# Revit family: FantiniCosmi_BIM_AP3102
name_source: partatom
category: Generic Models
units: mm (PartAtom-declared; Revit-internal decimal feet)

## family parameters
Always vertical = Yes
Can host rebar = No
Cut with Voids When Loaded = No
Part Type = Normal
Room Calculation Point = No
Round Connector Dimension = Use Diameter
Shared = No
Work Plane-Based = No

## types (1)
- Standard
    Air flow = 55 m³/h
    Catalog web link = https://www.fantinicosmi.it
    Comments = The fan starts operating when the light is switched on and continues to work for a programmable period of time (with a trimmer)
between 45 seconds and 20 minutes after the light is switched off
    Current = 0.1 A
    Default Elevation = 0 mm  [stored 0 ft]
    Description = Axial fan with high performance
    Designer = Carniti
    Ducting Ø = 120 mm / 5”
    Frequency = 50 Hz
    Humidity protection = IPX4
    Model = Aspirante (120)
    Part Number = AP3102 (Ø120mm)
    Power = 24 W
    Pt max = 9 mmH2O
    Sound Pressure 3Mt = 43 dB(A)
    Voltage = 230 V
    Weight = 0.7 Kg

note: [stored X ft] marks values corroborated as IEEE doubles in the binary element streams (Revit-internal decimal feet)

## geometry (parser evidence)
native form markers: Sweep x2
no freeform markers — native parametric forms only
